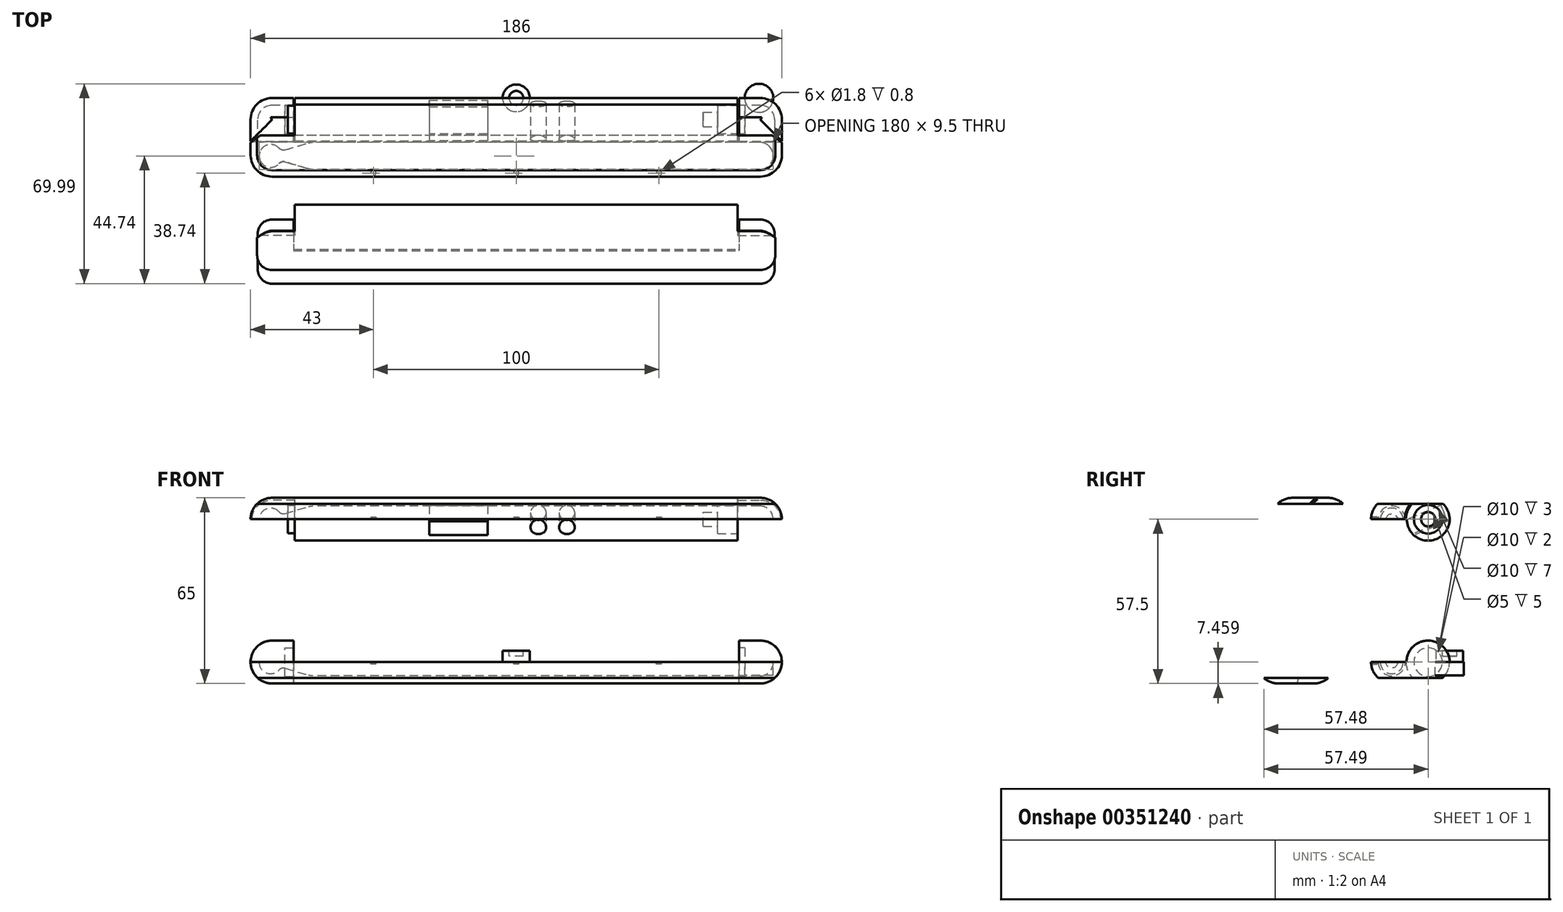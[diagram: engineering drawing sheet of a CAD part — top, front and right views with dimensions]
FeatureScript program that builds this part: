
annotation { "Feature Type Name" : "Feature", "Feature Type Description" : "" }
export const myFeature = defineFeature(function(context is Context, id is Id, definition is map)
    precondition{}
    {
        {
            var Q0;
            Q0=qCreatedBy(makeId("Front.planeOp"),FACE);
            var sketch = newSketch(context, id + "F0", { "sketchPlane" : qUnion([Q0])});
            skLineSegment(sketch, "E0.bottom", {"start": v(93, 7.5) * mm, "end": v(-93, 7.5) * mm});
            skLineSegment(sketch, "E0.top", {"start": v(93, -7.5) * mm, "end": v(-93, -7.5) * mm});
            skLineSegment(sketch, "E0.left", {"start": v(93, 7.5) * mm, "end": v(93, -7.5) * mm});
            skLineSegment(sketch, "E0.right", {"start": v(-93, 7.5) * mm, "end": v(-93, -7.5) * mm});
            skPoint(sketch, "E0.middle", {"position": v(0, 0) * mm});
            skSolve(sketch);
        }
        {
            var Q0;
            Q0=makeQuery(id+"F0.imprint","IMPRINT",FACE,{"disambiguationData":[TD([[makeQuery(id+"F0.imprint","IMPRINT",EDGE,{"derivedFrom":sQuery(id+"F0.wireOp",EDGE,"E0.bottom")}),1.0]])]});
            extrude(context, id + "F1", {"entities" : qUnion([Q0]), "depth" : 27.5 * mm});
        }
        {
            var Q0;
            Q0=makeQuery(id+"F1.opExtrude","CAP_EDGE",EDGE,{"disambiguationData":[OSD([sQuery(id+"F0.wireOp",EDGE,"E0.bottom")])],"isStart":false});
            var Q1;
            Q1=makeQuery(id+"F1.opExtrude","SWEPT_EDGE",EDGE,{"disambiguationData":[OSD([sQuery(id+"F0.wireOp",EDGE,"E0.bottom"),sQuery(id+"F0.wireOp",EDGE,"E0.left")])]});
            var Q2;
            Q2=makeQuery(id+"F1.opExtrude","CAP_EDGE",EDGE,{"disambiguationData":[OSD([sQuery(id+"F0.wireOp",EDGE,"E0.top")])],"isStart":false});
            var Q3;
            Q3=makeQuery(id+"F1.opExtrude","SWEPT_EDGE",EDGE,{"disambiguationData":[OSD([sQuery(id+"F0.wireOp",EDGE,"E0.top"),sQuery(id+"F0.wireOp",EDGE,"E0.left")])]});
            var Q4;
            Q4=makeQuery(id+"F1.opExtrude","CAP_EDGE",EDGE,{"disambiguationData":[OSD([sQuery(id+"F0.wireOp",EDGE,"E0.left")])],"isStart":false});
            var Q5;
            Q5=makeQuery(id+"F1.opExtrude","CAP_EDGE",EDGE,{"disambiguationData":[OSD([sQuery(id+"F0.wireOp",EDGE,"E0.bottom")])],"isStart":true});
            var Q6;
            Q6=makeQuery(id+"F1.opExtrude","CAP_EDGE",EDGE,{"disambiguationData":[OSD([sQuery(id+"F0.wireOp",EDGE,"E0.top")])],"isStart":true});
            var Q7;
            Q7=makeQuery(id+"F1.opExtrude","CAP_EDGE",EDGE,{"disambiguationData":[OSD([sQuery(id+"F0.wireOp",EDGE,"E0.left")])],"isStart":true});
            var Q8;
            Q8=makeQuery(id+"F1.opExtrude","CAP_EDGE",EDGE,{"disambiguationData":[OSD([sQuery(id+"F0.wireOp",EDGE,"E0.right")])],"isStart":true});
            var Q9;
            Q9=makeQuery(id+"F1.opExtrude","SWEPT_EDGE",EDGE,{"disambiguationData":[OSD([sQuery(id+"F0.wireOp",EDGE,"E0.bottom"),sQuery(id+"F0.wireOp",EDGE,"E0.right")])]});
            var Q10;
            Q10=makeQuery(id+"F1.opExtrude","SWEPT_EDGE",EDGE,{"disambiguationData":[OSD([sQuery(id+"F0.wireOp",EDGE,"E0.top"),sQuery(id+"F0.wireOp",EDGE,"E0.right")])]});
            var Q11;
            Q11=makeQuery(id+"F1.opExtrude","CAP_EDGE",EDGE,{"disambiguationData":[OSD([sQuery(id+"F0.wireOp",EDGE,"E0.right")])],"isStart":false});
            fillet(context, id + "F2", {"entities" : qUnion([Q0, Q1, Q2, Q3, Q4, Q5, Q6, Q7, Q8, Q9, Q10, Q11]), "radius" : 7.5 * mm, "tangentPropagation" : true, "allowEdgeOverflow" : false});
        }
        {
            var Q0;
            Q0=qCreatedBy(makeId("Right.planeOp"),FACE);
            cPlane(context, id + "F3", {"entities" : qUnion([Q0]), "cplaneType" : CPlaneType.OFFSET, "offset" : 78 * mm, "width" : 150 * mm, "height" : 150 * mm});
        }
        {
            var Q0;
            Q0=qCreatedBy(makeId("Front.planeOp"),FACE);
            var sketch = newSketch(context, id + "F4", { "sketchPlane" : qUnion([Q0])});
            skLineSegment(sketch, "E1", {"start": v(-72, 4.75) * mm, "end": v(85.25, 4.75) * mm});
            skLineSegment(sketch, "E2", {"start": v(-88, 0) * mm, "end": v(-72, 4.75) * mm});
            skArc(sketch, "E3", {"start": v(90, 0) * mm, "mid": v(88.6, 3.36) * mm, "end": v(85.25, 4.75) * mm});
            skLineSegment(sketch, "E4", {"start": v(-88, 0) * mm, "end": v(90, 0) * mm});
            skArc(sketch, "E5", {"start": v(-82, 0) * mm, "mid": v(-86, 4) * mm, "end": v(-90, 0) * mm});
            skLineSegment(sketch, "E6", {"start": v(-90, 0) * mm, "end": v(-82, 0) * mm});
            skSolve(sketch);
        }
        {
            var Q0;
            {var subQ0=sQuery(id+"F4.wireOp",EDGE,"E6");var subQ1=sQuery(id+"F4.wireOp",EDGE,"E2");var subQ2=makeQuery(id+"F4.imprint","INTERSECT",VERTEX,{"derivedFrom":[subQ1,subQ0]});Q0=makeQuery(id+"F4.imprint","IMPRINT",FACE,{"disambiguationData":[TD([[makeQuery(id+"F4.imprint","IMPRINT",EDGE,{"disambiguationData":[TD([[subQ2,-1.0]])],"derivedFrom":subQ1}),1.0]])]});}
            var Q1;
            {var subQ0=sQuery(id+"F4.wireOp",EDGE,"E6");var subQ1=sQuery(id+"F4.wireOp",EDGE,"E2");var subQ2=makeQuery(id+"F4.imprint","INTERSECT",VERTEX,{"derivedFrom":[subQ1,subQ0]});Q1=makeQuery(id+"F4.imprint","IMPRINT",FACE,{"disambiguationData":[TD([[makeQuery(id+"F4.imprint","IMPRINT",EDGE,{"disambiguationData":[TD([[subQ2,-1.0]])],"derivedFrom":subQ1}),-1.0]])]});}
            var Q2;
            {var subQ2=sQuery(id+"F4.wireOp",EDGE,"E1");Q2=makeQuery(id+"F4.imprint","IMPRINT",FACE,{"disambiguationData":[TD([[makeQuery(id+"F4.imprint","IMPRINT",EDGE,{"derivedFrom":subQ2}),-1.0]])]});}
            var Q3;
            Q3=sQuery(id+"F4.wireOp",EDGE,"E4");
            revolve(context, id + "F5", {"entities" : qUnion([Q0, Q1, Q2]), "axis" : qUnion([Q3]), "revolveType" : RevolveType.FULL});
        }
        {
            var Q0;
            Q0=makeQuery(id+"F5.opRevolve","SWEPT_EDGE",EDGE,{"disambiguationData":[OSD([sQuery(id+"F4.wireOp",EDGE,"E2"),sQuery(id+"F4.wireOp",EDGE,"E5")])]});
            fillet(context, id + "F6", {"entities" : qUnion([Q0]), "radius" : 2 * mm, "tangentPropagation" : true, "allowEdgeOverflow" : false});
        }
        {
            var Q0;
            Q0=makeQuery(id+"F5.opRevolve","SWEPT_EDGE",EDGE,{"disambiguationData":[OSD([sQuery(id+"F4.wireOp",EDGE,"E1"),sQuery(id+"F4.wireOp",EDGE,"E2")])]});
            fillet(context, id + "F7", {"entities" : qUnion([Q0]), "radius" : 5 * mm, "tangentPropagation" : true, "allowEdgeOverflow" : false});
        }
        {
            var Q0;
            Q0=qCreatedBy(makeId("Top.planeOp"),FACE);
            var sketch = newSketch(context, id + "F8", { "sketchPlane" : qUnion([Q0])});
            skCircle(sketch, "E7", {"center": v(85, 0) * mm, "radius": 5 * mm});
            skSolve(sketch);
        }
        {
            var Q0;
            Q0=makeQuery(id+"F8.imprint","IMPRINT",FACE,{"disambiguationData":[TD([[makeQuery(id+"F8.imprint","IMPRINT",EDGE,{"derivedFrom":sQuery(id+"F8.wireOp",EDGE,"E7")}),1.0]])]});
            extrude(context, id + "F9", {"entities" : qUnion([Q0]), "oppositeDirection" : true, "depth" : 4.75 * mm});
        }
        {
            var Q0;
            Q0=makeQuery(id+"F5.opRevolve","SWEPT_BODY",BODY,{"disambiguationData":[OSD([sQuery(id+"F4.wireOp",EDGE,"E1"),sQuery(id+"F4.wireOp",EDGE,"E2"),sQuery(id+"F4.wireOp",EDGE,"E3"),sQuery(id+"F4.wireOp",EDGE,"E4"),sQuery(id+"F4.wireOp",EDGE,"E5"),sQuery(id+"F4.wireOp",EDGE,"E6")])]});
            transform(context, id + "F10", {"entities" : qUnion([Q0]), "transformType" : TransformType.TRANSLATION_3D, "dx" : 0 * mm, "dy" : -20.25 * mm, "dz" : -0.1 * mm, "makeCopy" : false});
        }
        {
            var Q0;
            Q0=makeQuery(id+"F5.opRevolve","SWEPT_BODY",BODY,{"disambiguationData":[OSD([sQuery(id+"F4.wireOp",EDGE,"E1"),sQuery(id+"F4.wireOp",EDGE,"E2"),sQuery(id+"F4.wireOp",EDGE,"E3"),sQuery(id+"F4.wireOp",EDGE,"E4"),sQuery(id+"F4.wireOp",EDGE,"E5"),sQuery(id+"F4.wireOp",EDGE,"E6")])]});
            var Q1;
            Q1=makeQuery(id+"F1.opExtrude","SWEPT_BODY",BODY,{"disambiguationData":[OSD([sQuery(id+"F0.wireOp",EDGE,"E0.bottom"),sQuery(id+"F0.wireOp",EDGE,"E0.top"),sQuery(id+"F0.wireOp",EDGE,"E0.left"),sQuery(id+"F0.wireOp",EDGE,"E0.right")])]});
            booleanBodies(context, id + "F11", {"operationType" : BooleanOperationType.SUBTRACTION, "tools" : qUnion([Q0]), "targets" : qUnion([Q1]), "keepTools" : true});
        }
        {
            var Q0;
            Q0=makeQuery(id+"F1.opExtrude","SWEPT_BODY",BODY,{"disambiguationData":[OSD([sQuery(id+"F0.wireOp",EDGE,"E0.bottom"),sQuery(id+"F0.wireOp",EDGE,"E0.top"),sQuery(id+"F0.wireOp",EDGE,"E0.left"),sQuery(id+"F0.wireOp",EDGE,"E0.right")])]});
            transform(context, id + "F12", {"entities" : qUnion([Q0]), "transformType" : TransformType.TRANSLATION_3D, "dx" : 0 * mm, "dy" : 0 * mm, "dz" : 50 * mm, "makeCopy" : true});
        }
        {
            var Q0;
            Q0=qCreatedBy(makeId("Right.planeOp"),FACE);
            cPlane(context, id + "F13", {"entities" : qUnion([Q0]), "cplaneType" : CPlaneType.OFFSET, "offset" : 93 * mm, "width" : 150 * mm, "height" : 150 * mm});
        }
        {
            var Q0;
            Q0=qCreatedBy(makeId("Right.planeOp"),FACE);
            cPlane(context, id + "F14", {"entities" : qUnion([Q0]), "cplaneType" : CPlaneType.OFFSET, "offset" : 93 * mm, "oppositeDirection" : true, "width" : 150 * mm, "height" : 150 * mm});
        }
        {
            var Q0;
            Q0=qCreatedBy(id+"F13.planeOp",FACE);
            var sketch = newSketch(context, id + "F15", { "sketchPlane" : qUnion([Q0])});
            skCircle(sketch, "E8", {"center": v(-7.6, 0) * mm, "radius": 7.5 * mm});
            skLineSegment(sketch, "E9.bottom", {"start": v(-6.72, 0) * mm, "end": v(-52.07, 0) * mm});
            skLineSegment(sketch, "E9.top", {"start": v(-6.72, 20.65) * mm, "end": v(-52.07, 20.65) * mm});
            skLineSegment(sketch, "E9.left", {"start": v(-6.72, 0) * mm, "end": v(-6.72, 20.65) * mm});
            skLineSegment(sketch, "E9.right", {"start": v(-52.07, 0) * mm, "end": v(-52.07, 20.65) * mm});
            skPoint(sketch, "E9.middle", {"position": v(-29.4, 10.33) * mm});
            skSolve(sketch);
        }
        {
            var Q0;
            {var subQ1=sQuery(id+"F15.wireOp",EDGE,"E9.top");Q0=makeQuery(id+"F15.imprint","IMPRINT",FACE,{"disambiguationData":[TD([[makeQuery(id+"F15.imprint","IMPRINT",EDGE,{"derivedFrom":subQ1}),1.0]])]});}
            extrude(context, id + "F16", {"entities" : qUnion([Q0]), "operationType" : NewBodyOperationType.REMOVE, "endBound" : BoundingType.THROUGH_ALL, "oppositeDirection" : true, "depth" : 25 * mm});
        }
        {
            var Q0;
            Q0=qCreatedBy(id+"F13.planeOp",FACE);
            var sketch = newSketch(context, id + "F17", { "sketchPlane" : qUnion([Q0])});
            skCircle(sketch, "E10", {"center": v(-7.5, 50) * mm, "radius": 7.5 * mm});
            skLineSegment(sketch, "E11.bottom", {"start": v(-7.5, 50) * mm, "end": v(-34.83, 50) * mm});
            skLineSegment(sketch, "E11.top", {"start": v(-7.5, 41.08) * mm, "end": v(-34.83, 41.08) * mm});
            skLineSegment(sketch, "E11.left", {"start": v(-7.5, 50) * mm, "end": v(-7.5, 41.08) * mm});
            skLineSegment(sketch, "E11.right", {"start": v(-34.83, 50) * mm, "end": v(-34.83, 41.08) * mm});
            skSolve(sketch);
        }
        {
            var Q0;
            {var subQ1=sQuery(id+"F17.wireOp",EDGE,"E11.top");Q0=makeQuery(id+"F17.imprint","IMPRINT",FACE,{"disambiguationData":[TD([[makeQuery(id+"F17.imprint","IMPRINT",EDGE,{"derivedFrom":subQ1}),-1.0]])]});}
            extrude(context, id + "F18", {"entities" : qUnion([Q0]), "operationType" : NewBodyOperationType.REMOVE, "endBound" : BoundingType.THROUGH_ALL, "oppositeDirection" : true, "depth" : 25 * mm});
        }
        {
            var Q0;
            Q0=qCreatedBy(id+"F13.planeOp",FACE);
            var sketch = newSketch(context, id + "F19", { "sketchPlane" : qUnion([Q0])});
            skCircle(sketch, "E12", {"center": v(-7.5, 50) * mm, "radius": 7.8 * mm});
            skSolve(sketch);
        }
        {
            var Q0;
            Q0=makeQuery(id+"F19.imprint","IMPRINT",FACE,{"disambiguationData":[TD([[makeQuery(id+"F19.imprint","IMPRINT",EDGE,{"derivedFrom":sQuery(id+"F19.wireOp",EDGE,"E12")}),1.0]])]});
            extrude(context, id + "F20", {"entities" : qUnion([Q0]), "operationType" : NewBodyOperationType.REMOVE, "oppositeDirection" : true, "depth" : 15.5 * mm});
        }
        {
            var Q0;
            Q0=qCreatedBy(id+"F14.planeOp",FACE);
            var sketch = newSketch(context, id + "F21", { "sketchPlane" : qUnion([Q0])});
            skCircle(sketch, "E13", {"center": v(-7.5, 50) * mm, "radius": 7.8 * mm});
            skSolve(sketch);
        }
        {
            var Q0;
            Q0=makeQuery(id+"F21.imprint","IMPRINT",FACE,{"disambiguationData":[TD([[makeQuery(id+"F21.imprint","IMPRINT",EDGE,{"derivedFrom":sQuery(id+"F21.wireOp",EDGE,"E13")}),1.0]])]});
            extrude(context, id + "F22", {"entities" : qUnion([Q0]), "operationType" : NewBodyOperationType.REMOVE, "depth" : 15.5 * mm});
        }
        {
            var Q0;
            Q0=qCreatedBy(id+"F3.planeOp",FACE);
            var sketch = newSketch(context, id + "F23", { "sketchPlane" : qUnion([Q0])});
            skCircle(sketch, "E14", {"center": v(-7.5, 0) * mm, "radius": 7.75 * mm});
            skSolve(sketch);
        }
        {
            var Q0;
            Q0=makeQuery(id+"F23.imprint","IMPRINT",FACE,{"disambiguationData":[TD([[makeQuery(id+"F23.imprint","IMPRINT",EDGE,{"derivedFrom":sQuery(id+"F23.wireOp",EDGE,"E14")}),1.0]])]});
            extrude(context, id + "F24", {"entities" : qUnion([Q0]), "oppositeDirection" : true, "depth" : 156 * mm});
        }
        {
            var Q0;
            Q0=makeQuery(id+"F24.opExtrude","SWEPT_BODY",BODY,{"disambiguationData":[OSD([sQuery(id+"F23.wireOp",EDGE,"E14")])]});
            var Q1;
            Q1=makeQuery(id+"F1.opExtrude","SWEPT_BODY",BODY,{"disambiguationData":[OSD([sQuery(id+"F0.wireOp",EDGE,"E0.bottom"),sQuery(id+"F0.wireOp",EDGE,"E0.top"),sQuery(id+"F0.wireOp",EDGE,"E0.left"),sQuery(id+"F0.wireOp",EDGE,"E0.right")])]});
            booleanBodies(context, id + "F25", {"operationType" : BooleanOperationType.SUBTRACTION, "tools" : qUnion([Q0]), "targets" : qUnion([Q1])});
        }
        {
            var Q0;
            Q0=qCreatedBy(makeId("Front.planeOp"),FACE);
            cPlane(context, id + "F26", {"entities" : qUnion([Q0]), "cplaneType" : CPlaneType.OFFSET, "offset" : 16 * mm, "width" : 150 * mm, "height" : 150 * mm});
        }
        {
            var Q0;
            Q0=qCreatedBy(id+"F26.planeOp",FACE);
            var sketch = newSketch(context, id + "F27", { "sketchPlane" : qUnion([Q0])});
            skLineSegment(sketch, "E15.bottom", {"start": v(-30.5, 50) * mm, "end": v(-10, 50) * mm});
            skLineSegment(sketch, "E15.top", {"start": v(-30.5, 44) * mm, "end": v(-10, 44) * mm});
            skLineSegment(sketch, "E15.left", {"start": v(-30.5, 50) * mm, "end": v(-30.5, 44) * mm});
            skLineSegment(sketch, "E15.right", {"start": v(-10, 50) * mm, "end": v(-10, 44) * mm});
            skCircle(sketch, "E16", {"center": v(7.75, 47.25) * mm, "radius": 2.75 * mm});
            skCircle(sketch, "E17", {"center": v(17.75, 47.25) * mm, "radius": 2.75 * mm});
            skSolve(sketch);
        }
        {
            var Q0;
            Q0=makeQuery(id+"F27.imprint","IMPRINT",FACE,{"disambiguationData":[TD([[makeQuery(id+"F27.imprint","IMPRINT",EDGE,{"derivedFrom":sQuery(id+"F27.wireOp",EDGE,"E15.bottom")}),-1.0]])]});
            var Q1;
            Q1=makeQuery(id+"F27.imprint","IMPRINT",FACE,{"disambiguationData":[TD([[makeQuery(id+"F27.imprint","IMPRINT",EDGE,{"derivedFrom":sQuery(id+"F27.wireOp",EDGE,"E16")}),1.0]])]});
            var Q2;
            Q2=makeQuery(id+"F27.imprint","IMPRINT",FACE,{"disambiguationData":[TD([[makeQuery(id+"F27.imprint","IMPRINT",EDGE,{"derivedFrom":sQuery(id+"F27.wireOp",EDGE,"E17")}),1.0]])]});
            extrude(context, id + "F28", {"entities" : qUnion([Q0, Q1, Q2]), "oppositeDirection" : true, "depth" : 14 * mm});
        }
        {
            var Q0;
            Q0=makeQuery(id+"F28.opExtrude","SWEPT_BODY",BODY,{"disambiguationData":[OSD([sQuery(id+"F27.wireOp",EDGE,"E15.bottom"),sQuery(id+"F27.wireOp",EDGE,"E15.top"),sQuery(id+"F27.wireOp",EDGE,"E15.left"),sQuery(id+"F27.wireOp",EDGE,"E15.right")])]});
            var Q1;
            Q1=makeQuery(id+"F28.opExtrude","SWEPT_BODY",BODY,{"disambiguationData":[OSD([sQuery(id+"F27.wireOp",EDGE,"E16")])]});
            var Q2;
            Q2=makeQuery(id+"F28.opExtrude","SWEPT_BODY",BODY,{"disambiguationData":[OSD([sQuery(id+"F27.wireOp",EDGE,"E17")])]});
            var Q3;
            Q3=makeQuery(id+"F28.opExtrude","CAP_EDGE",EDGE,{"disambiguationData":[OSD([sQuery(id+"F27.wireOp",EDGE,"E15.bottom")])],"isStart":true});
            transform(context, id + "F29", {"entities" : qUnion([Q0, Q1, Q2]), "transformType" : TransformType.ROTATION, "transformAxis" : qUnion([Q3]), "angle" : 22.33 * degree, "makeCopy" : false});
        }
        {
            var Q0;
            Q0=makeQuery(id+"F28.opExtrude","SWEPT_BODY",BODY,{"disambiguationData":[OSD([sQuery(id+"F27.wireOp",EDGE,"E15.bottom"),sQuery(id+"F27.wireOp",EDGE,"E15.top"),sQuery(id+"F27.wireOp",EDGE,"E15.left"),sQuery(id+"F27.wireOp",EDGE,"E15.right")])]});
            transform(context, id + "F30", {"entities" : qUnion([Q0]), "transformType" : TransformType.TRANSLATION_3D, "dx" : 0 * mm, "dy" : 0 * mm, "dz" : -0.5 * mm, "makeCopy" : false});
        }
        {
            var Q0;
            Q0=makeQuery(id+"F28.opExtrude","SWEPT_BODY",BODY,{"disambiguationData":[OSD([sQuery(id+"F27.wireOp",EDGE,"E16")])]});
            transform(context, id + "F31", {"entities" : qUnion([Q0]), "transformType" : TransformType.TRANSLATION_3D, "dx" : 0 * mm, "dy" : 0 * mm, "dz" : -0.5 * mm, "makeCopy" : false});
        }
        {
            var Q0;
            Q0=makeQuery(id+"F28.opExtrude","SWEPT_BODY",BODY,{"disambiguationData":[OSD([sQuery(id+"F27.wireOp",EDGE,"E17")])]});
            transform(context, id + "F32", {"entities" : qUnion([Q0]), "transformType" : TransformType.TRANSLATION_3D, "dx" : 0 * mm, "dy" : 0 * mm, "dz" : -0.5 * mm, "makeCopy" : false});
        }
        {
            var Q0;
            Q0=makeQuery(id+"F28.opExtrude","SWEPT_BODY",BODY,{"disambiguationData":[OSD([sQuery(id+"F27.wireOp",EDGE,"E15.bottom"),sQuery(id+"F27.wireOp",EDGE,"E15.top"),sQuery(id+"F27.wireOp",EDGE,"E15.left"),sQuery(id+"F27.wireOp",EDGE,"E15.right")])]});
            var Q1;
            Q1=makeQuery(id+"F28.opExtrude","SWEPT_BODY",BODY,{"disambiguationData":[OSD([sQuery(id+"F27.wireOp",EDGE,"E16")])]});
            var Q2;
            Q2=makeQuery(id+"F28.opExtrude","SWEPT_BODY",BODY,{"disambiguationData":[OSD([sQuery(id+"F27.wireOp",EDGE,"E17")])]});
            var Q3;
            Q3=makeQuery(id+"F12.opPattern","COPY",BODY,{"derivedFrom":makeQuery(id+"F1.opExtrude","SWEPT_BODY",BODY,{"disambiguationData":[OSD([sQuery(id+"F0.wireOp",EDGE,"E0.bottom"),sQuery(id+"F0.wireOp",EDGE,"E0.top"),sQuery(id+"F0.wireOp",EDGE,"E0.left"),sQuery(id+"F0.wireOp",EDGE,"E0.right")])]}),"instanceName":"1"});
            booleanBodies(context, id + "F33", {"operationType" : BooleanOperationType.SUBTRACTION, "tools" : qUnion([Q0, Q1, Q2]), "targets" : qUnion([Q3])});
        }
        {
            var Q0;
            Q0=makeQuery(id+"F25.opBoolean","COPY",FACE,{"derivedFrom":makeQuery(id+"F24.opExtrude","CAP_FACE",FACE,{"disambiguationData":[OSD([sQuery(id+"F23.wireOp",EDGE,"E14")])],"isStart":false})});
            var sketch = newSketch(context, id + "F34", { "sketchPlane" : qUnion([Q0])});
            skCircle(sketch, "E18", {"center": v(-7.51, -0.04) * mm, "radius": 5 * mm});
            skSolve(sketch);
        }
        {
            var Q0;
            Q0=makeQuery(id+"F34.imprint","IMPRINT",FACE,{"disambiguationData":[TD([[makeQuery(id+"F34.imprint","IMPRINT",EDGE,{"derivedFrom":sQuery(id+"F34.wireOp",EDGE,"E18")}),1.0]])]});
            extrude(context, id + "F35", {"entities" : qUnion([Q0]), "operationType" : NewBodyOperationType.REMOVE, "oppositeDirection" : true, "depth" : 3 * mm});
        }
        {
            var Q0;
            Q0=makeQuery(id+"F20.boolean.opBoolean","COPY",FACE,{"derivedFrom":makeQuery(id+"F20.opExtrude","CAP_FACE",FACE,{"disambiguationData":[OSD([sQuery(id+"F19.wireOp",EDGE,"E12")])],"isStart":false})});
            var sketch = newSketch(context, id + "F36", { "sketchPlane" : qUnion([Q0])});
            skCircle(sketch, "E19", {"center": v(-7.5, 50) * mm, "radius": 5 * mm});
            skSolve(sketch);
        }
        {
            var Q0;
            Q0=makeQuery(id+"F36.imprint","IMPRINT",FACE,{"disambiguationData":[TD([[makeQuery(id+"F36.imprint","IMPRINT",EDGE,{"derivedFrom":sQuery(id+"F36.wireOp",EDGE,"E19")}),1.0]])]});
            extrude(context, id + "F37", {"entities" : qUnion([Q0]), "operationType" : NewBodyOperationType.REMOVE, "oppositeDirection" : true, "depth" : 7 * mm});
        }
        {
            var Q0;
            Q0=makeQuery(id+"F22.boolean.opBoolean","COPY",FACE,{"derivedFrom":makeQuery(id+"F22.opExtrude","CAP_FACE",FACE,{"disambiguationData":[OSD([sQuery(id+"F21.wireOp",EDGE,"E13")])],"isStart":false})});
            var sketch = newSketch(context, id + "F38", { "sketchPlane" : qUnion([Q0])});
            skCircle(sketch, "E20", {"center": v(7.5, 50) * mm, "radius": 4.9 * mm});
            skSolve(sketch);
        }
        {
            var Q0;
            Q0=makeQuery(id+"F38.imprint","IMPRINT",FACE,{"disambiguationData":[TD([[makeQuery(id+"F38.imprint","IMPRINT",EDGE,{"derivedFrom":sQuery(id+"F38.wireOp",EDGE,"E20")}),1.0]])]});
            extrude(context, id + "F39", {"entities" : qUnion([Q0]), "operationType" : NewBodyOperationType.ADD, "depth" : 2.5 * mm});
        }
        {
            var Q0;
            Q0=makeQuery(id+"F25.opBoolean","COPY",FACE,{"derivedFrom":makeQuery(id+"F24.opExtrude","CAP_FACE",FACE,{"disambiguationData":[OSD([sQuery(id+"F23.wireOp",EDGE,"E14")])],"isStart":true})});
            var sketch = newSketch(context, id + "F40", { "sketchPlane" : qUnion([Q0])});
            skCircle(sketch, "E21", {"center": v(7.51, -0.04) * mm, "radius": 5 * mm});
            skSolve(sketch);
        }
        {
            var Q0;
            Q0=makeQuery(id+"F40.imprint","IMPRINT",FACE,{"disambiguationData":[TD([[makeQuery(id+"F40.imprint","IMPRINT",EDGE,{"derivedFrom":sQuery(id+"F40.wireOp",EDGE,"E21")}),1.0]])]});
            extrude(context, id + "F41", {"entities" : qUnion([Q0]), "operationType" : NewBodyOperationType.REMOVE, "oppositeDirection" : true, "depth" : 2 * mm});
        }
        {
            var Q0;
            Q0=makeQuery(id+"F16.boolean.opBoolean","COPY",FACE,{"derivedFrom":makeQuery(id+"F16.opExtrude","SWEPT_FACE",FACE,{"disambiguationData":[OSD([sQuery(id+"F15.wireOp",EDGE,"E9.bottom")])]})});
            var sketch = newSketch(context, id + "F42", { "sketchPlane" : qUnion([Q0])});
            skCircle(sketch, "E22", {"center": v(0, -26.25) * mm, "radius": 0.9 * mm});
            skCircle(sketch, "E23", {"center": v(-50, -26.25) * mm, "radius": 0.9 * mm});
            skCircle(sketch, "E24", {"center": v(50, -26.25) * mm, "radius": 0.9 * mm});
            skSolve(sketch);
        }
        {
            var Q0;
            Q0=makeQuery(id+"F42.imprint","IMPRINT",FACE,{"disambiguationData":[TD([[makeQuery(id+"F42.imprint","IMPRINT",EDGE,{"derivedFrom":sQuery(id+"F42.wireOp",EDGE,"E24")}),1.0]])]});
            var Q1;
            Q1=makeQuery(id+"F42.imprint","IMPRINT",FACE,{"disambiguationData":[TD([[makeQuery(id+"F42.imprint","IMPRINT",EDGE,{"derivedFrom":sQuery(id+"F42.wireOp",EDGE,"E22")}),1.0]])]});
            var Q2;
            Q2=makeQuery(id+"F42.imprint","IMPRINT",FACE,{"disambiguationData":[TD([[makeQuery(id+"F42.imprint","IMPRINT",EDGE,{"derivedFrom":sQuery(id+"F42.wireOp",EDGE,"E23")}),1.0]])]});
            extrude(context, id + "F43", {"entities" : qUnion([Q0, Q1, Q2]), "operationType" : NewBodyOperationType.REMOVE, "oppositeDirection" : true, "depth" : 0.8 * mm});
        }
        {
            var Q0;
            Q0=makeQuery(id+"F18.boolean.opBoolean","COPY",FACE,{"derivedFrom":makeQuery(id+"F18.opExtrude","SWEPT_FACE",FACE,{"disambiguationData":[OSD([sQuery(id+"F17.wireOp",EDGE,"E11.bottom")])]})});
            var sketch = newSketch(context, id + "F44", { "sketchPlane" : qUnion([Q0])});
            skCircle(sketch, "E25", {"center": v(-50, 26.25) * mm, "radius": 0.9 * mm});
            skCircle(sketch, "E26", {"center": v(0, 26.25) * mm, "radius": 0.9 * mm});
            skCircle(sketch, "E27", {"center": v(50, 26.25) * mm, "radius": 0.9 * mm});
            skSolve(sketch);
        }
        {
            var Q0;
            Q0=makeQuery(id+"F44.imprint","IMPRINT",FACE,{"disambiguationData":[TD([[makeQuery(id+"F44.imprint","IMPRINT",EDGE,{"derivedFrom":sQuery(id+"F44.wireOp",EDGE,"E25")}),1.0]])]});
            var Q1;
            Q1=makeQuery(id+"F44.imprint","IMPRINT",FACE,{"disambiguationData":[TD([[makeQuery(id+"F44.imprint","IMPRINT",EDGE,{"derivedFrom":sQuery(id+"F44.wireOp",EDGE,"E26")}),1.0]])]});
            var Q2;
            Q2=makeQuery(id+"F44.imprint","IMPRINT",FACE,{"disambiguationData":[TD([[makeQuery(id+"F44.imprint","IMPRINT",EDGE,{"derivedFrom":sQuery(id+"F44.wireOp",EDGE,"E27")}),1.0]])]});
            extrude(context, id + "F45", {"entities" : qUnion([Q0, Q1, Q2]), "operationType" : NewBodyOperationType.REMOVE, "oppositeDirection" : true, "depth" : 0.8 * mm});
        }
        {
            var Q0;
            Q0=makeQuery(id+"F37.boolean.opBoolean","COPY",FACE,{"derivedFrom":makeQuery(id+"F37.opExtrude","CAP_FACE",FACE,{"disambiguationData":[OSD([sQuery(id+"F36.wireOp",EDGE,"E19")])],"isStart":false})});
            var sketch = newSketch(context, id + "F46", { "sketchPlane" : qUnion([Q0])});
            skCircle(sketch, "E28", {"center": v(-7.5, 50) * mm, "radius": 2.5 * mm});
            skSolve(sketch);
        }
        {
            var Q0;
            Q0=makeQuery(id+"F46.imprint","IMPRINT",FACE,{"disambiguationData":[TD([[makeQuery(id+"F46.imprint","IMPRINT",EDGE,{"derivedFrom":sQuery(id+"F46.wireOp",EDGE,"E28")}),1.0]])]});
            extrude(context, id + "F47", {"entities" : qUnion([Q0]), "operationType" : NewBodyOperationType.REMOVE, "oppositeDirection" : true, "depth" : 5 * mm});
        }
        {
            var Q0;
            Q0=qCreatedBy(makeId("Top.planeOp"),FACE);
            var sketch = newSketch(context, id + "F48", { "sketchPlane" : qUnion([Q0])});
            skCircle(sketch, "E29", {"center": v(0, 0) * mm, "radius": 4.75 * mm});
            skSolve(sketch);
        }
        {
            var Q0;
            Q0=makeQuery(id+"F48.imprint","IMPRINT",FACE,{"disambiguationData":[TD([[makeQuery(id+"F48.imprint","IMPRINT",EDGE,{"derivedFrom":sQuery(id+"F48.wireOp",EDGE,"E29")}),1.0]])]});
            extrude(context, id + "F49", {"entities" : qUnion([Q0]), "depth" : 4 * mm});
        }
        {
            var Q0;
            Q0=makeQuery(id+"F49.opExtrude","CAP_FACE",FACE,{"disambiguationData":[OSD([sQuery(id+"F48.wireOp",EDGE,"E29")])],"isStart":false});
            var sketch = newSketch(context, id + "F50", { "sketchPlane" : qUnion([Q0])});
            skCircle(sketch, "E30", {"center": v(0, 0) * mm, "radius": 2.5 * mm});
            skSolve(sketch);
        }
        {
            var Q0;
            Q0=makeQuery(id+"F50.imprint","IMPRINT",FACE,{"disambiguationData":[TD([[makeQuery(id+"F50.imprint","IMPRINT",EDGE,{"derivedFrom":sQuery(id+"F50.wireOp",EDGE,"E30")}),1.0]])]});
            extrude(context, id + "F51", {"entities" : qUnion([Q0]), "operationType" : NewBodyOperationType.REMOVE, "oppositeDirection" : true, "depth" : 2 * mm});
        }
        {
            var Q0;
            Q0=makeQuery(id+"F25.opBoolean","INTERSECT",EDGE,{"derivedFrom":[makeQuery(id+"F1.opExtrude","SWEPT_FACE",FACE,{"disambiguationData":[OSD([sQuery(id+"F0.wireOp",EDGE,"E0.top")])]}),makeQuery(id+"F24.opExtrude","SWEPT_FACE",FACE,{"disambiguationData":[OSD([sQuery(id+"F23.wireOp",EDGE,"E14")])]})]});
            chamfer(context, id + "F52", {"entities" : qUnion([Q0]), "width" : 4 * mm, "tangentPropagation" : true});
        }
        {
            var Q0;
            Q0=makeQuery(id+"F20.boolean.opBoolean","INTERSECT",EDGE,{"derivedFrom":[makeQuery(id+"F12.opPattern","COPY",FACE,{"derivedFrom":makeQuery(id+"F1.opExtrude","SWEPT_FACE",FACE,{"disambiguationData":[OSD([sQuery(id+"F0.wireOp",EDGE,"E0.bottom")])]}),"instanceName":"1"}),makeQuery(id+"F20.opExtrude","SWEPT_FACE",FACE,{"disambiguationData":[OSD([sQuery(id+"F19.wireOp",EDGE,"E12")])]})]});
            var Q1;
            Q1=makeQuery(id+"F22.boolean.opBoolean","INTERSECT",EDGE,{"derivedFrom":[makeQuery(id+"F12.opPattern","COPY",FACE,{"derivedFrom":makeQuery(id+"F1.opExtrude","SWEPT_FACE",FACE,{"disambiguationData":[OSD([sQuery(id+"F0.wireOp",EDGE,"E0.bottom")])]}),"instanceName":"1"}),makeQuery(id+"F22.opExtrude","SWEPT_FACE",FACE,{"disambiguationData":[OSD([sQuery(id+"F21.wireOp",EDGE,"E13")])]})]});
            chamfer(context, id + "F53", {"entities" : qUnion([Q0, Q1]), "width" : 2 * mm, "tangentPropagation" : true});
        }
        {
            var Q0;
            Q0=qCreatedBy(makeId("Top.planeOp"),FACE);
            cPlane(context, id + "F54", {"entities" : qUnion([Q0]), "cplaneType" : CPlaneType.OFFSET, "offset" : 5.6 * mm, "oppositeDirection" : true, "width" : 150 * mm, "height" : 150 * mm});
        }
        {
            var Q0;
            Q0=makeQuery(id+"F1.opExtrude","SWEPT_BODY",BODY,{"disambiguationData":[OSD([sQuery(id+"F0.wireOp",EDGE,"E0.bottom"),sQuery(id+"F0.wireOp",EDGE,"E0.top"),sQuery(id+"F0.wireOp",EDGE,"E0.left"),sQuery(id+"F0.wireOp",EDGE,"E0.right")])]});
            transform(context, id + "F55", {"entities" : qUnion([Q0]), "transformType" : TransformType.TRANSLATION_3D, "dx" : 0 * mm, "dy" : -40 * mm, "dz" : 0 * mm, "makeCopy" : true});
        }
        {
            var Q0;
            Q0=qCreatedBy(id+"F54.planeOp",FACE);
            var sketch = newSketch(context, id + "F56", { "sketchPlane" : qUnion([Q0])});
            skLineSegment(sketch, "E31.bottom", {"start": v(-98.05, -34.69) * mm, "end": v(102.5, -34.69) * mm});
            skLineSegment(sketch, "E31.top", {"start": v(-98.05, -81.97) * mm, "end": v(102.5, -81.97) * mm});
            skLineSegment(sketch, "E31.left", {"start": v(-98.05, -34.69) * mm, "end": v(-98.05, -81.97) * mm});
            skLineSegment(sketch, "E31.right", {"start": v(102.5, -34.69) * mm, "end": v(102.5, -81.97) * mm});
            skSolve(sketch);
        }
        {
            var Q0;
            Q0=makeQuery(id+"F56.imprint","IMPRINT",FACE,{"disambiguationData":[TD([[makeQuery(id+"F56.imprint","IMPRINT",EDGE,{"derivedFrom":sQuery(id+"F56.wireOp",EDGE,"E31.bottom")}),-1.0]])]});
            extrude(context, id + "F57", {"entities" : qUnion([Q0]), "operationType" : NewBodyOperationType.REMOVE, "depth" : 25 * mm});
        }
        {
            var Q0;
            Q0=qCreatedBy(id+"F54.planeOp",FACE);
            var sketch = newSketch(context, id + "F58", { "sketchPlane" : qUnion([Q0])});
            skLineSegment(sketch, "E32.bottom", {"start": v(-98.5, 4.45) * mm, "end": v(100.94, 4.45) * mm});
            skLineSegment(sketch, "E32.top", {"start": v(-98.5, -33.04) * mm, "end": v(100.94, -33.04) * mm});
            skLineSegment(sketch, "E32.left", {"start": v(-98.5, 4.45) * mm, "end": v(-98.5, -33.04) * mm});
            skLineSegment(sketch, "E32.right", {"start": v(100.94, 4.45) * mm, "end": v(100.94, -33.04) * mm});
            skSolve(sketch);
        }
        {
            var Q0;
            Q0=makeQuery(id+"F58.imprint","IMPRINT",FACE,{"disambiguationData":[TD([[makeQuery(id+"F58.imprint","IMPRINT",EDGE,{"derivedFrom":sQuery(id+"F58.wireOp",EDGE,"E32.bottom")}),-1.0]])]});
            extrude(context, id + "F59", {"entities" : qUnion([Q0]), "operationType" : NewBodyOperationType.REMOVE, "oppositeDirection" : true, "depth" : 25 * mm});
        }
        {
            var Q0;
            Q0=qCreatedBy(makeId("Top.planeOp"),FACE);
            cPlane(context, id + "F60", {"entities" : qUnion([Q0]), "cplaneType" : CPlaneType.OFFSET, "offset" : 55.4 * mm, "width" : 150 * mm, "height" : 150 * mm});
        }
        {
            var Q0;
            Q0=makeQuery(id+"F12.opPattern","COPY",BODY,{"derivedFrom":makeQuery(id+"F1.opExtrude","SWEPT_BODY",BODY,{"disambiguationData":[OSD([sQuery(id+"F0.wireOp",EDGE,"E0.bottom"),sQuery(id+"F0.wireOp",EDGE,"E0.top"),sQuery(id+"F0.wireOp",EDGE,"E0.left"),sQuery(id+"F0.wireOp",EDGE,"E0.right")])]}),"instanceName":"1"});
            transform(context, id + "F61", {"entities" : qUnion([Q0]), "transformType" : TransformType.TRANSLATION_3D, "dx" : 0 * mm, "dy" : -35 * mm, "dz" : 0 * mm, "makeCopy" : true});
        }
        {
            var Q0;
            Q0=qCreatedBy(id+"F60.planeOp",FACE);
            var sketch = newSketch(context, id + "F62", { "sketchPlane" : qUnion([Q0])});
            skLineSegment(sketch, "E33.bottom", {"start": v(-100.21, -31.5) * mm, "end": v(104.02, -31.5) * mm});
            skLineSegment(sketch, "E33.top", {"start": v(-100.21, -67.62) * mm, "end": v(104.02, -67.62) * mm});
            skLineSegment(sketch, "E33.left", {"start": v(-100.21, -31.5) * mm, "end": v(-100.21, -67.62) * mm});
            skLineSegment(sketch, "E33.right", {"start": v(104.02, -31.5) * mm, "end": v(104.02, -67.62) * mm});
            skSolve(sketch);
        }
        {
            var Q0;
            Q0=makeQuery(id+"F62.imprint","IMPRINT",FACE,{"disambiguationData":[TD([[makeQuery(id+"F62.imprint","IMPRINT",EDGE,{"derivedFrom":sQuery(id+"F62.wireOp",EDGE,"E33.bottom")}),-1.0]])]});
            extrude(context, id + "F63", {"entities" : qUnion([Q0]), "operationType" : NewBodyOperationType.REMOVE, "oppositeDirection" : true, "depth" : 25 * mm});
        }
        {
            var Q0;
            Q0=qCreatedBy(id+"F60.planeOp",FACE);
            var sketch = newSketch(context, id + "F64", { "sketchPlane" : qUnion([Q0])});
            skLineSegment(sketch, "E34.bottom", {"start": v(-102.27, 5.14) * mm, "end": v(100.43, 5.14) * mm});
            skLineSegment(sketch, "E34.top", {"start": v(-102.27, -31.5) * mm, "end": v(100.43, -31.5) * mm});
            skLineSegment(sketch, "E34.left", {"start": v(-102.27, 5.14) * mm, "end": v(-102.27, -31.5) * mm});
            skLineSegment(sketch, "E34.right", {"start": v(100.43, 5.14) * mm, "end": v(100.43, -31.5) * mm});
            skSolve(sketch);
        }
        {
            var Q0;
            Q0=makeQuery(id+"F64.imprint","IMPRINT",FACE,{"disambiguationData":[TD([[makeQuery(id+"F64.imprint","IMPRINT",EDGE,{"derivedFrom":sQuery(id+"F64.wireOp",EDGE,"E34.bottom")}),-1.0]])]});
            extrude(context, id + "F65", {"entities" : qUnion([Q0]), "operationType" : NewBodyOperationType.REMOVE, "depth" : 25 * mm});
        }
    });
